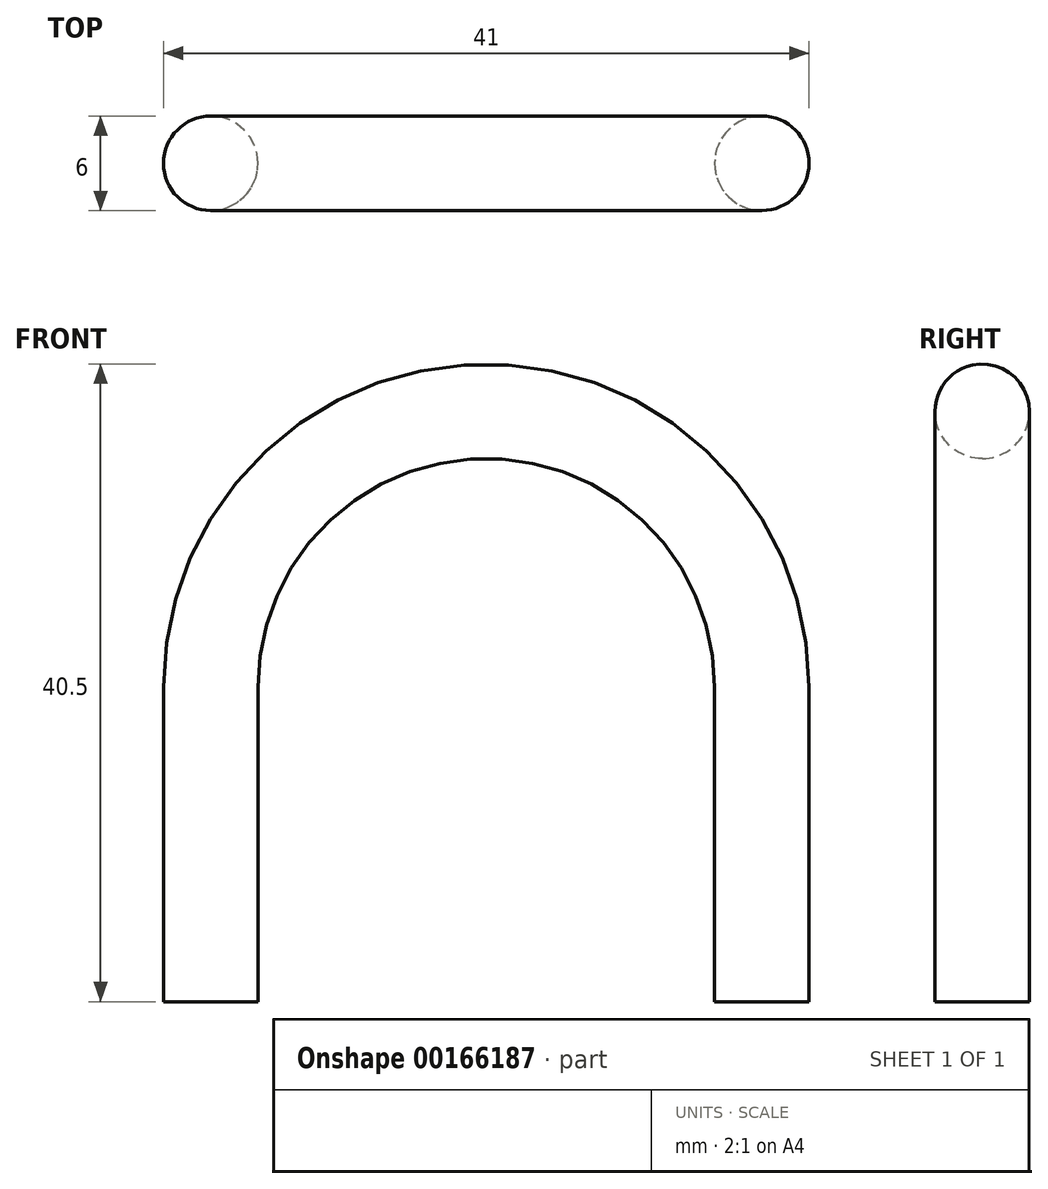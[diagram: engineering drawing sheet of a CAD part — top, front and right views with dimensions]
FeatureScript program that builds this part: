
annotation { "Feature Type Name" : "Feature", "Feature Type Description" : "" }
export const myFeature = defineFeature(function(context is Context, id is Id, definition is map)
    precondition{}
    {
        {
            var Q0;
            Q0=qCreatedBy(makeId("Front.planeOp"),FACE);
            var sketch = newSketch(context, id + "F0", { "sketchPlane" : qUnion([Q0])});
            skLineSegment(sketch, "E0", {"start": v(0, 0) * mm, "end": v(0, 20) * mm});
            skLineSegment(sketch, "E1", {"start": v(35, 20) * mm, "end": v(35, 0) * mm});
            skArc(sketch, "E2", {"start": v(35, 20) * mm, "mid": v(17.5, 37.5) * mm, "end": v(0, 20) * mm});
            skSolve(sketch);
        }
        {
            var Q0;
            Q0=qCreatedBy(makeId("Top.planeOp"),FACE);
            var sketch = newSketch(context, id + "F1", { "sketchPlane" : qUnion([Q0])});
            skCircle(sketch, "E3", {"center": v(0, 0) * mm, "radius": 3 * mm});
            skSolve(sketch);
        }
        {
            var Q0;
            Q0=makeQuery(id+"F1.imprint","IMPRINT",FACE,{"disambiguationData":[TD([[makeQuery(id+"F1.imprint","IMPRINT",EDGE,{"derivedFrom":sQuery(id+"F1.wireOp",EDGE,"E3")}),1.0]])]});
            var Q1;
            Q1=sQuery(id+"F0.wireOp",EDGE,"E0");
            var Q2;
            Q2=sQuery(id+"F0.wireOp",EDGE,"E2");
            var Q3;
            Q3=sQuery(id+"F0.wireOp",EDGE,"E1");
            sweep(context, id + "F2", {"profiles" : qUnion([Q0]), "path" : qUnion([Q1, Q2, Q3])});
        }
    });
